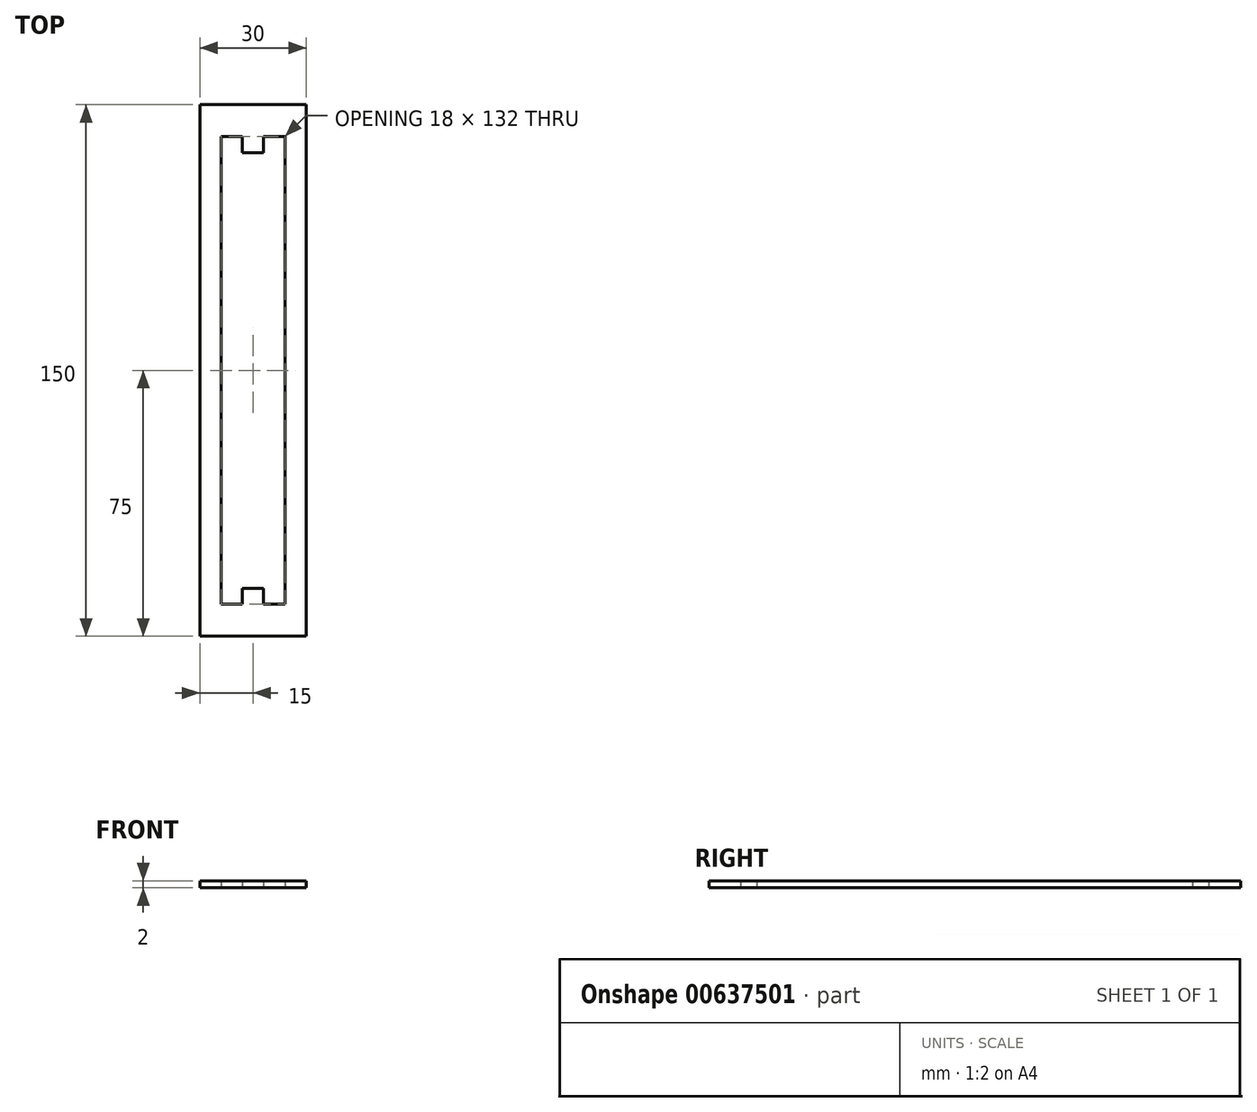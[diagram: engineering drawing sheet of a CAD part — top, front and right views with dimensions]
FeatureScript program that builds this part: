
annotation { "Feature Type Name" : "Feature", "Feature Type Description" : "" }
export const myFeature = defineFeature(function(context is Context, id is Id, definition is map)
    precondition{}
    {
        {
            var Q0;
            Q0=qCreatedBy(makeId("Top.planeOp"),FACE);
            var sketch = newSketch(context, id + "F0", { "sketchPlane" : qUnion([Q0])});
            skLineSegment(sketch, "E0.bottom", {"start": v(0, 0) * mm, "end": v(30, 0) * mm});
            skLineSegment(sketch, "E0.top", {"start": v(0, 150) * mm, "end": v(30, 150) * mm});
            skLineSegment(sketch, "E0.left", {"start": v(0, 0) * mm, "end": v(0, 150) * mm});
            skLineSegment(sketch, "E0.right", {"start": v(30, 0) * mm, "end": v(30, 150) * mm});
            skLineSegment(sketch, "E1", {"start": v(6, 141) * mm, "end": v(12, 141) * mm});
            skLineSegment(sketch, "E2", {"start": v(24, 141) * mm, "end": v(24, 9) * mm});
            skLineSegment(sketch, "E3", {"start": v(6, 141) * mm, "end": v(6, 9) * mm});
            skLineSegment(sketch, "E4", {"start": v(6, 9) * mm, "end": v(12, 9) * mm});
            skLineSegment(sketch, "E5", {"start": v(18, 141) * mm, "end": v(18, 136.5) * mm});
            skLineSegment(sketch, "E6", {"start": v(18, 136.5) * mm, "end": v(12, 136.5) * mm});
            skLineSegment(sketch, "E7", {"start": v(12, 136.5) * mm, "end": v(12, 141) * mm});
            skLineSegment(sketch, "E8", {"start": v(12, 9) * mm, "end": v(12, 13.5) * mm});
            skLineSegment(sketch, "E9", {"start": v(12, 13.5) * mm, "end": v(18, 13.5) * mm});
            skLineSegment(sketch, "E10", {"start": v(18, 13.5) * mm, "end": v(18, 9) * mm});
            skLineSegment(sketch, "E11.trimOffspring", {"start": v(18, 9) * mm, "end": v(24, 9) * mm});
            skLineSegment(sketch, "E12.trimOffspring", {"start": v(18, 141) * mm, "end": v(24, 141) * mm});
            skSolve(sketch);
        }
        {
            var Q0;
            Q0 = qSketchRegion(id + "F0", true);
            extrude(context, id + "F1", {"entities" : qUnion([Q0]), "depth" : 2 * mm, "offsetDistance" : 25 * mm});
        }
    });
